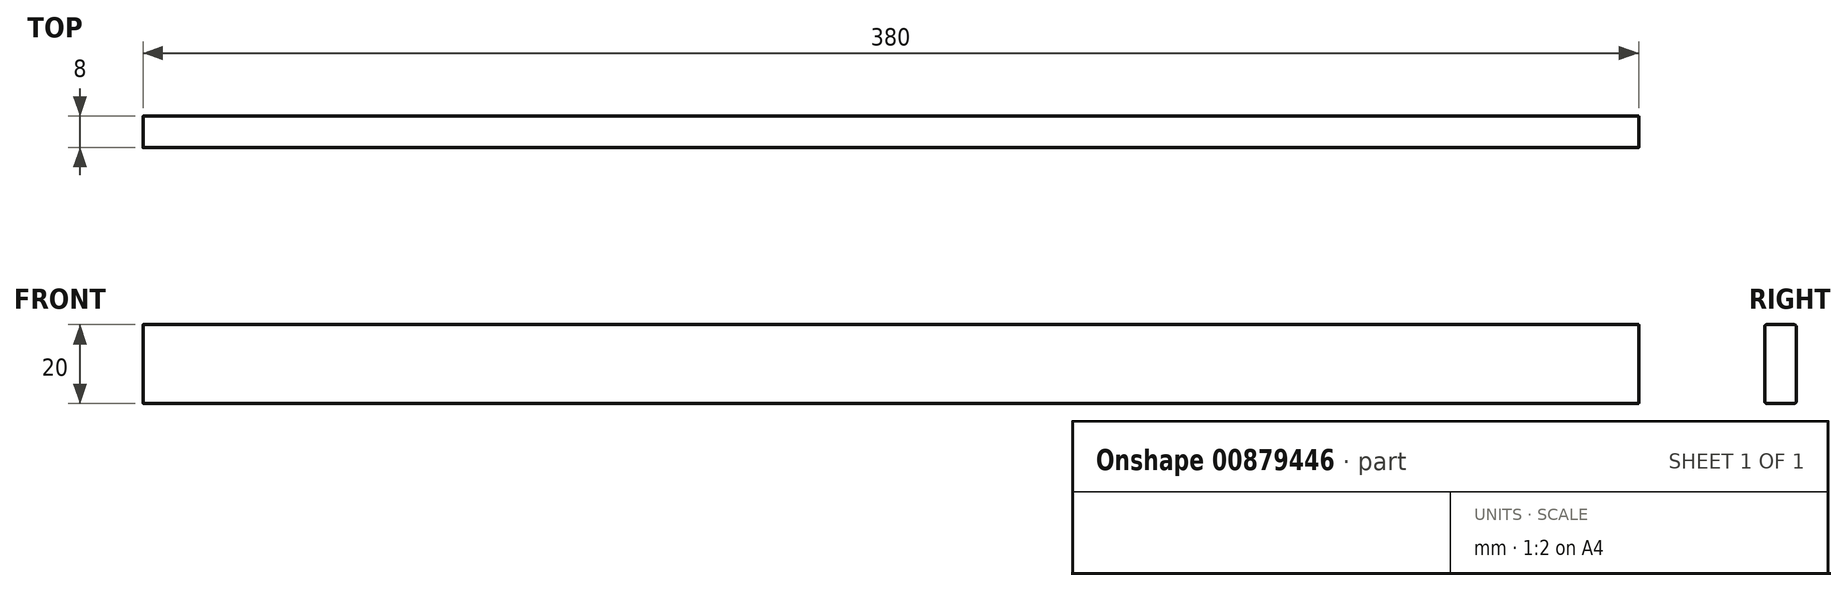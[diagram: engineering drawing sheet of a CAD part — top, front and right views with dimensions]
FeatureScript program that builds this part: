
annotation { "Feature Type Name" : "Feature", "Feature Type Description" : "" }
export const myFeature = defineFeature(function(context is Context, id is Id, definition is map)
    precondition{}
    {
        {
            var Q0;
            Q0=qCreatedBy(makeId("Front.planeOp"),FACE);
            var sketch = newSketch(context, id + "F0", { "sketchPlane" : qUnion([Q0])});
            skLineSegment(sketch, "E0.bottom", {"start": v(-190, 10) * mm, "end": v(190, 10) * mm});
            skLineSegment(sketch, "E0.top", {"start": v(-190, -10) * mm, "end": v(190, -10) * mm});
            skLineSegment(sketch, "E0.left", {"start": v(-190, 10) * mm, "end": v(-190, -10) * mm});
            skLineSegment(sketch, "E0.right", {"start": v(190, 10) * mm, "end": v(190, -10) * mm});
            skPoint(sketch, "E0.middle", {"position": v(0, 0) * mm});
            skSolve(sketch);
        }
        {
            var Q0;
            Q0=makeQuery(id+"F0.imprint","IMPRINT",FACE,{"disambiguationData":[TD([[makeQuery(id+"F0.imprint","IMPRINT",EDGE,{"derivedFrom":sQuery(id+"F0.wireOp",EDGE,"E0.bottom")}),-1.0]])]});
            extrude(context, id + "F1", {"entities" : qUnion([Q0]), "flatOperationType" : FlatOperationType.REMOVE, "depth" : 8 * mm, "offsetDistance" : 25 * mm, "domain" : OperationDomain.MODEL});
        }
        {
            var Q0;
            Q0=makeQuery(id+"F1.opExtrude","CAP_EDGE",EDGE,{"disambiguationData":[OSD([sQuery(id+"F0.wireOp",EDGE,"E0.bottom")])],"isStart":false});
            var Q1;
            Q1=makeQuery(id+"F1.opExtrude","CAP_EDGE",EDGE,{"disambiguationData":[OSD([sQuery(id+"F0.wireOp",EDGE,"E0.bottom")])],"isStart":true});
            var Q2;
            Q2=makeQuery(id+"F1.opExtrude","CAP_EDGE",EDGE,{"disambiguationData":[OSD([sQuery(id+"F0.wireOp",EDGE,"E0.top")])],"isStart":true});
            var Q3;
            Q3=makeQuery(id+"F1.opExtrude","CAP_EDGE",EDGE,{"disambiguationData":[OSD([sQuery(id+"F0.wireOp",EDGE,"E0.top")])],"isStart":false});
            fillet(context, id + "F2", {"entities" : qUnion([Q0, Q1, Q2, Q3]), "radius" : 0.5 * mm, "tangentPropagation" : true, "defaultsChanged" : false, "allowEdgeOverflow" : false, "vertexSettings" : []});
        }
    });
